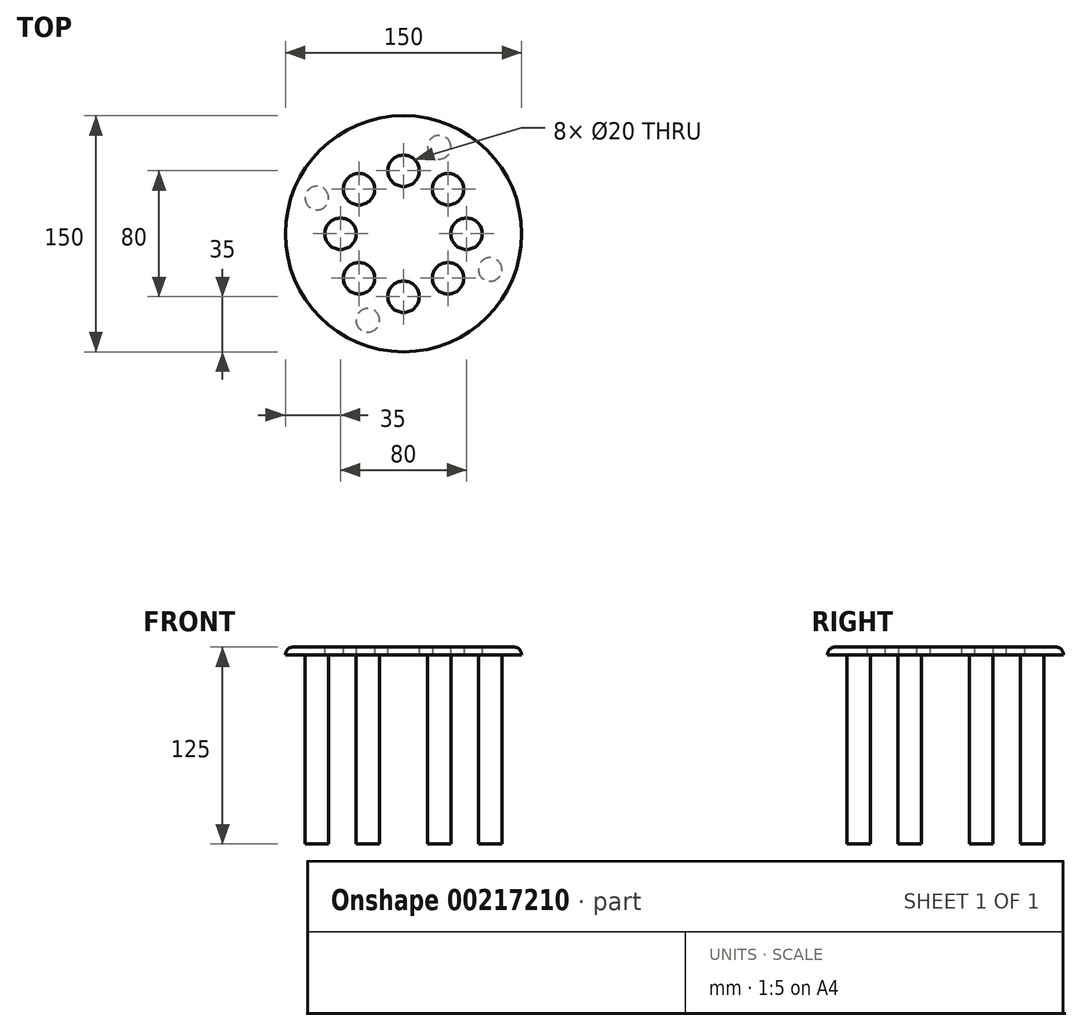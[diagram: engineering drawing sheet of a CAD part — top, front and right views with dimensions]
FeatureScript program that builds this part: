
annotation { "Feature Type Name" : "Feature", "Feature Type Description" : "" }
export const myFeature = defineFeature(function(context is Context, id is Id, definition is map)
    precondition{}
    {
        {
            var Q0;
            Q0=qCreatedBy(makeId("Top.planeOp"),FACE);
            var sketch = newSketch(context, id + "F0", { "sketchPlane" : qUnion([Q0])});
            skCircle(sketch, "E0", {"center": v(0, 0) * mm, "radius": 75 * mm});
            skCircle(sketch, "E1", {"center": v(0, 40) * mm, "radius": 10 * mm});
            skCircle(sketch, "E2.1.0", {"center": v(-28.28, 28.28) * mm, "radius": 10 * mm});
            skCircle(sketch, "E2.2.0", {"center": v(-40, 0) * mm, "radius": 10 * mm});
            skCircle(sketch, "E2.3.0", {"center": v(-28.28, -28.28) * mm, "radius": 10 * mm});
            skCircle(sketch, "E2.4.0", {"center": v(0, -40) * mm, "radius": 10 * mm});
            skCircle(sketch, "E2.5.0", {"center": v(28.28, -28.28) * mm, "radius": 10 * mm});
            skCircle(sketch, "E2.6.0", {"center": v(40, 0) * mm, "radius": 10 * mm});
            skCircle(sketch, "E2.7.0", {"center": v(28.28, 28.28) * mm, "radius": 10 * mm});
            skSolve(sketch);
        }
        {
            var Q0;
            Q0=makeQuery(id+"F0.imprint","IMPRINT",FACE,{"disambiguationData":[TD([[makeQuery(id+"F0.imprint","IMPRINT",EDGE,{"derivedFrom":sQuery(id+"F0.wireOp",EDGE,"E0")}),1.0]])]});
            extrude(context, id + "F1", {"entities" : qUnion([Q0]), "depth" : 5 * mm});
        }
        {
            var Q0;
            Q0=makeQuery(id+"F1.opExtrude","CAP_EDGE",EDGE,{"disambiguationData":[OSD([sQuery(id+"F0.wireOp",EDGE,"E0")])],"isStart":false});
            fillet(context, id + "F2", {"entities" : qUnion([Q0]), "radius" : 5 * mm, "tangentPropagation" : true, "allowEdgeOverflow" : false});
        }
        {
            var Q0;
            Q0=makeQuery(id+"F1.opExtrude","CAP_FACE",FACE,{"disambiguationData":[OSD([sQuery(id+"F0.wireOp",EDGE,"E0"),sQuery(id+"F0.wireOp",EDGE,"E1"),sQuery(id+"F0.wireOp",EDGE,"E2.1.0"),sQuery(id+"F0.wireOp",EDGE,"E2.2.0"),sQuery(id+"F0.wireOp",EDGE,"E2.3.0"),sQuery(id+"F0.wireOp",EDGE,"E2.4.0"),sQuery(id+"F0.wireOp",EDGE,"E2.5.0"),sQuery(id+"F0.wireOp",EDGE,"E2.6.0"),sQuery(id+"F0.wireOp",EDGE,"E2.7.0")])],"isStart":true});
            var sketch = newSketch(context, id + "F3", { "sketchPlane" : qUnion([Q0])});
            skCircle(sketch, "E3", {"center": v(-22.66, 55) * mm, "radius": 7.5 * mm});
            skCircle(sketch, "E4.1.0", {"center": v(-55, -22.66) * mm, "radius": 7.5 * mm});
            skCircle(sketch, "E4.2.0", {"center": v(22.66, -55) * mm, "radius": 7.5 * mm});
            skCircle(sketch, "E4.3.0", {"center": v(55, 22.66) * mm, "radius": 7.5 * mm});
            skPoint(sketch, "E4.center", {"position": v(0, 0) * mm});
            skSolve(sketch);
        }
        {
            var Q0;
            Q0 = qSketchRegion(id + "F3", true);
            extrude(context, id + "F4", {"entities" : qUnion([Q0]), "operationType" : NewBodyOperationType.ADD, "depth" : 120 * mm});
        }
    });
